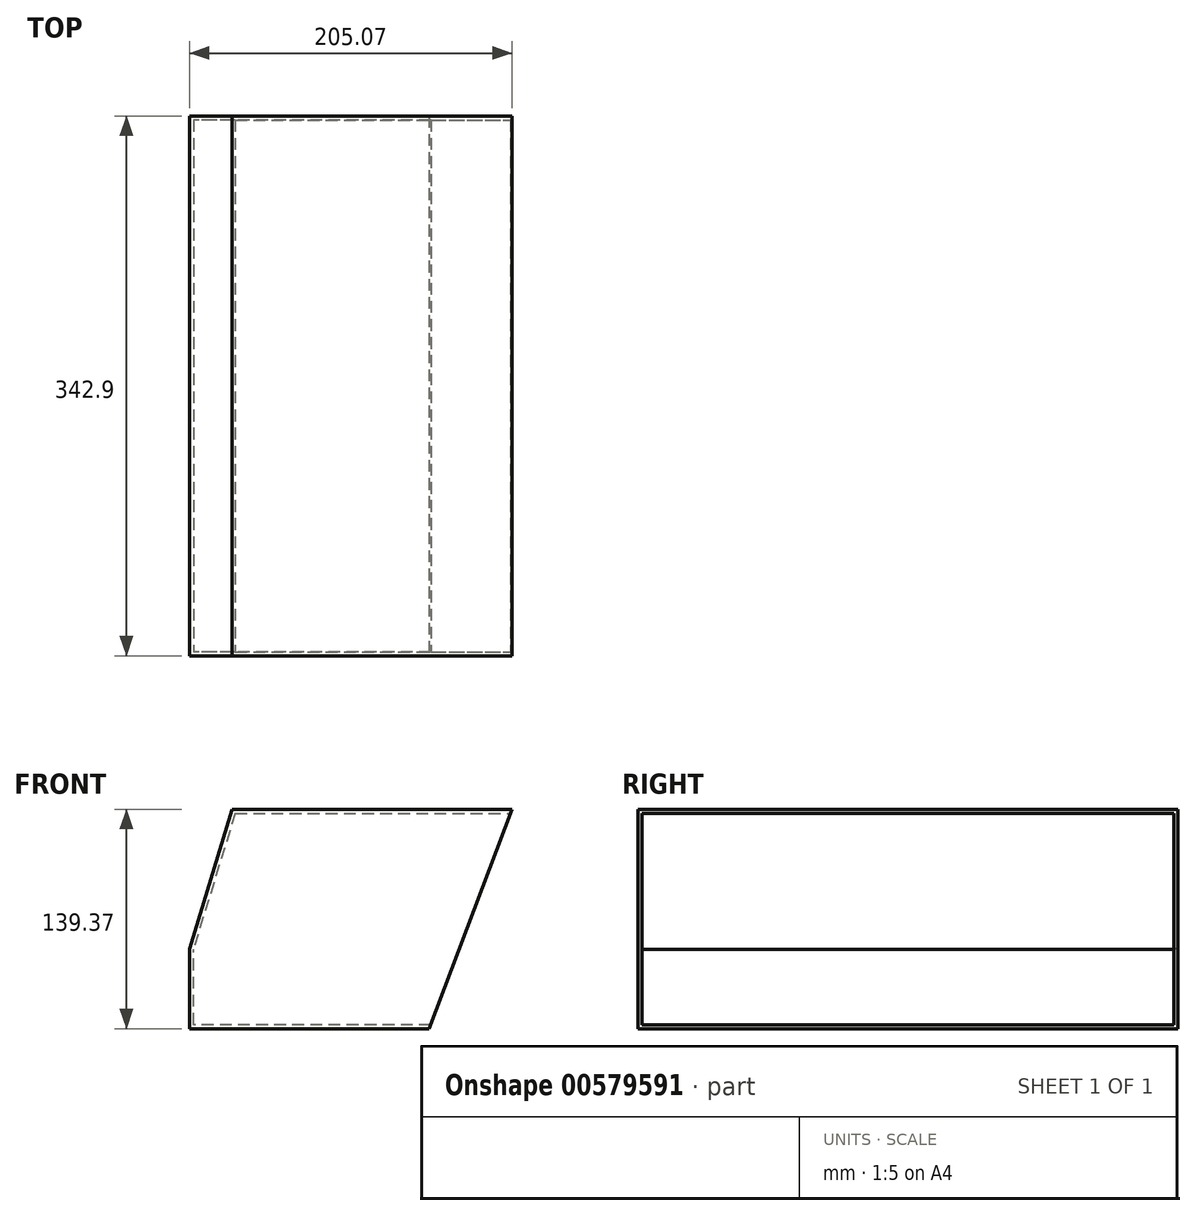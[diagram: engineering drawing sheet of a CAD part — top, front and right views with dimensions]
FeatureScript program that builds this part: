
annotation { "Feature Type Name" : "Feature", "Feature Type Description" : "" }
export const myFeature = defineFeature(function(context is Context, id is Id, definition is map)
    precondition{}
    {
        {
            var Q0;
            Q0=qCreatedBy(makeId("Front.planeOp"),FACE);
            var sketch = newSketch(context, id + "F0", { "sketchPlane" : qUnion([Q0])});
            skLineSegment(sketch, "E0.top", {"start": v(61.56, 139.7) * mm, "end": v(239.36, 139.7) * mm});
            skLineSegment(sketch, "E1", {"start": v(186.69, 0.33) * mm, "end": v(239.36, 139.7) * mm});
            skPoint(sketch, "E2.start.orphan", {"position": v(0, 47.4) * mm});
            skLineSegment(sketch, "E3", {"start": v(186.69, 0.33) * mm, "end": v(34.29, 0.33) * mm});
            skLineSegment(sketch, "E4", {"start": v(34.29, 0.33) * mm, "end": v(34.29, 51.13) * mm});
            skLineSegment(sketch, "E5", {"start": v(61.56, 139.7) * mm, "end": v(34.29, 51.13) * mm});
            skPoint(sketch, "E6.start.orphan", {"position": v(0, 0) * mm});
            skPoint(sketch, "E7.start.orphan", {"position": v(0, 94.8) * mm});
            skSolve(sketch);
        }
        {
            var Q0;
            Q0=makeQuery(id+"F0.imprint","IMPRINT",FACE,{"disambiguationData":[TD([[makeQuery(id+"F0.imprint","IMPRINT",EDGE,{"derivedFrom":sQuery(id+"F0.wireOp",EDGE,"E0.top")}),-1.0]])]});
            extrude(context, id + "F1", {"entities" : qUnion([Q0]), "oppositeDirection" : true, "depth" : 342.9 * mm, "offsetDistance" : 25.4 * mm});
        }
        {
            var Q0;
            Q0=makeQuery(id+"F1.opExtrude","SWEPT_FACE",FACE,{"disambiguationData":[OSD([sQuery(id+"F0.wireOp",EDGE,"E1")])]});
            shell(context, id + "F2", {"entities" : qUnion([Q0]), "thickness" : 2.54 * mm});
        }
    });
